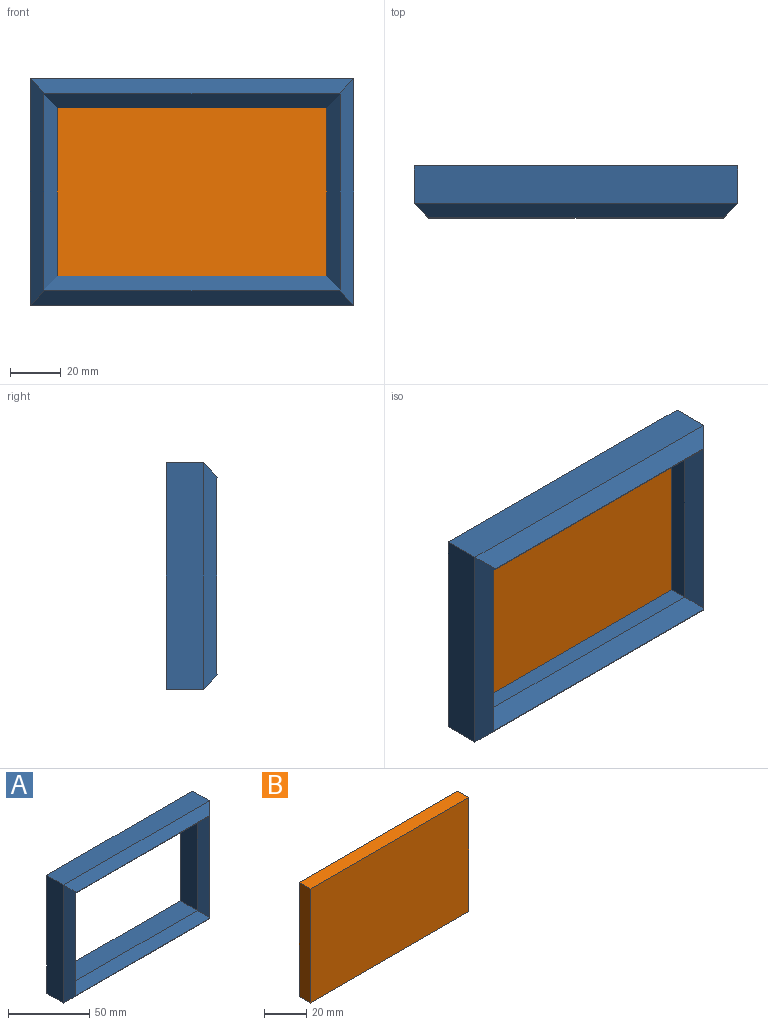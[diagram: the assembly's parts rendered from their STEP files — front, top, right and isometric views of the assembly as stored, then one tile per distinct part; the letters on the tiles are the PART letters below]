
ASSEMBLY  parts=2 mates=1
PART A: 19 faces, bbox 127x20.3x88.9 mm
  f0: plane 115.82x0.25mm, normal (0,-1,0), area 29.4mm2, adj f12,f13,f16,f17
  f1: plane 127x14.73mm, normal (0,0,1), area 1871mm2, adj f2,f8,f10,f11
  f2: plane 88.9x14.73mm, normal (-1,0,0), area 1309.7mm2, adj f1,f3,f10,f13
  f3: plane 127x14.73mm, normal (0,0,-1), area 1871mm2, adj f2,f8,f10,f12
  f4: plane 66.04x14.73mm, normal (1,0,0), area 972.9mm2, adj f5,f7,f10,f14
  f5: plane 106.08x14.73mm, normal (0,0,-1), area 1562.7mm2, adj f4,f6,f10,f15
  f6: plane 66.04x14.73mm, normal (-1,0,0), area 972.9mm2, adj f5,f7,f10,f18
  f7: plane 106.08x14.73mm, normal (0,0,1), area 1562.7mm2, adj f4,f6,f10,f17
  f8: plane 88.9x14.73mm, normal (1,0,0), area 1309.7mm2, adj f1,f3,f10,f16
  f9: plane 115.82x0.25mm, normal (0,-1,0), area 29.4mm2, adj f11,f13,f15,f16
  f10: plane 127x88.9mm, normal (0,1,0), area 4284.9mm2, adj f1,f2,f3,f4,f5,f6,f7,f8
  f11: plane 127x5.59mm, normal (0,-0.71,0.71), area 959.5mm2, adj f1,f9,f13,f16
  f12: plane 127x5.59mm, normal (0,-0.71,-0.71), area 959.5mm2, adj f0,f3,f13,f16
  f13: plane 88.9x5.59mm, normal (-0.71,-0.71,0), area 619.5mm2, adj f0,f2,f9,f11,f12,f14,f15,f17
  f14: plane 76.5x5.23mm, normal (0.71,-0.71,0), area 527.2mm2, adj f4,f13,f15,f17
  f15: plane 116.54x5.59mm, normal (0,-0.71,-0.71), area 882.1mm2, adj f5,f9,f13,f14,f16,f18
  f16: plane 88.9x5.59mm, normal (0.71,-0.71,0), area 619.5mm2, adj f0,f8,f9,f11,f12,f15,f17,f18
  f17: plane 116.54x5.59mm, normal (0,-0.71,0.71), area 882.1mm2, adj f0,f7,f13,f14,f16,f18
  f18: plane 76.5x5.23mm, normal (-0.71,-0.71,0), area 527.2mm2, adj f6,f15,f16,f17
PART B: 6 faces, bbox 106.1x7.6x66 mm
  f0: plane 106.07x7.62mm, normal (0,0,1), area 808.3mm2, adj f1,f3,f4,f5
  f1: plane 66.04x7.62mm, normal (-1,0,0), area 503.2mm2, adj f0,f2,f4,f5
  f2: plane 106.07x7.62mm, normal (0,0,-1), area 808.3mm2, adj f1,f3,f4,f5
  f3: plane 66.04x7.62mm, normal (1,0,0), area 503.2mm2, adj f0,f2,f4,f5
  f4: plane 106.07x66.04mm, normal (0,-1,0), area 7004.9mm2, adj f0,f1,f2,f3
  f5: plane 106.07x66.04mm, normal (0,1,0), area 7004.9mm2, adj f0,f1,f2,f3
PLACE A t=(0,7.62,0)mm
PLACE B t=(0,7.62,0)mm
MATE fastened A.f10 <-> B.f5  axis (0,1,0) through (0,7.62,33.02)mm
